# Revit family: Grohe_ShowerRailSet_261642433
name_source: partatom
category: Plumbing Fixtures
units: mm (PartAtom-declared; Revit-internal decimal feet)

## family parameters
Cut with Voids When Loaded = No
Host = Face
OmniClass Number = 23.45.05.00
OmniClass Title = Sanitary Equipment
Part Type = Normal
Room Calculation Point = No
Round Connector Dimension = Use Diameter
Shared = No

## types (1)
- Shower Rail Set (261642433)
    Assembly Code = D2013
    AssetType = Fixed
    BIMObjectName = Grohe_ShowerRailSet_261642433
    CO2NeutralProduction = GROHE is one of the first leading manufacturer within the sanitary industry having a CO2-neutral production.
    ClassificationName = Uniclass2015
    ClassificationValue = Pr_40_20_87_55
    Color = Grohe_Chrome
    Cost = 0 $
    Default Elevation = 0 mm  [stored 0 ft]
    Description = Shower Rail Set
    DimensionsDocumentLink = https://cdn.cloud.grohe.com
    DocumentationCertificates = https://www.bimstore.co
    DocumentationInstallationGuide = https://www.bimstore.co
    DocumentationLiterature = https://www.bimstore.co
    DocumentationMaintenance = https://www.bimstore.co
    DocumentationTechnical = https://www.bimstore.co
    DurationUnit = Years
    Ecojoy = No
    ExpectedLife = 0
    Finish = Chrome
    FullRecyclabilityOfPlastic = All plastic components are fully recycable
    GROHESocialCommittment = green.grohe.com/social_engagement
    GROHESustainability = green.grohe.com
    IfcExportAs = IfcPipeFitting
    IfcExportType = IfcPipeFittingType
    Keynote = N16
    Manufacturer = Grohe
    ManufacturerName = Grohe
    Model = Shower Rail Set
    ModelNumber = 261642433
    ModelReference = Shower Rail Set
    NBSDescription = Shower fittings package
    NBSObjectName = Grohe - Shower fittings package
    NBSReference = 45-35-70/298
    NominalDepth = 0 mm  [stored 0 ft]
    NominalHeight = 0 mm  [stored 0 ft]
    NominalLength = 0 mm  [stored 0 ft]
    PrimaryMaterial = Grohe_Chrome
    ProductDescription = consisting of:

hand shower Tempesta 110 (26 161)

wall shower holder Tempesta, non-adjustable (28 605)

shower hose Relexaflex 1250 mm 1/2" x 1/2" (28 150)

GROHE Water Saving - Less water, perfect flow

GROHE SmartSwitch - easily rotate the dial to enjoy your preferred spray option

GROHE DreamSpray perfect spray pattern

GROHE Long-Life finish

SpeedClean anti-limescale system

Inner WaterGuide - inner insulation for surface and scalding protection

ShockProof silicone ring prevents damages caused by shower falling

maximum flow rate (at 3 bar): 8.5 l/min

min. recommended pressure 1.0 bar

suitable for instantaneous heater

professional exclusive
    ProductNumber = 261642433
    ProductShortText = Wall holder set 2 sprays (Rain, Jet)
    ProductType = Shower Set
    ProductionYear = 2023
    SustainabilityAward = green.grohe.com/awards
    SustainabilityReport = green.grohe.com/reporting
    TPIDocumentLink = https://cdn.cloud.grohe.com
    Type Comments = Shower Rail Set
    TypeName = Shower Rail Set
    URL = https://www.grohe.co.uk
    WarrantyDurationLabor = 0
    WarrantyDurationParts = 0
    WarrantyDurationUnit = Years
    _BSBibleVersion = 17
    _BimSpecGuid = 0
    _CurrentRevision = 1
    _DistributedBy = https://www.bimstore.co
    _ObjectUserGuide = https://www.bimstore.co

note: [stored X ft] marks values corroborated as IEEE doubles in the binary element streams (Revit-internal decimal feet)

## geometry (parser evidence)
native form markers: Sweep x2
no freeform markers — native parametric forms only
